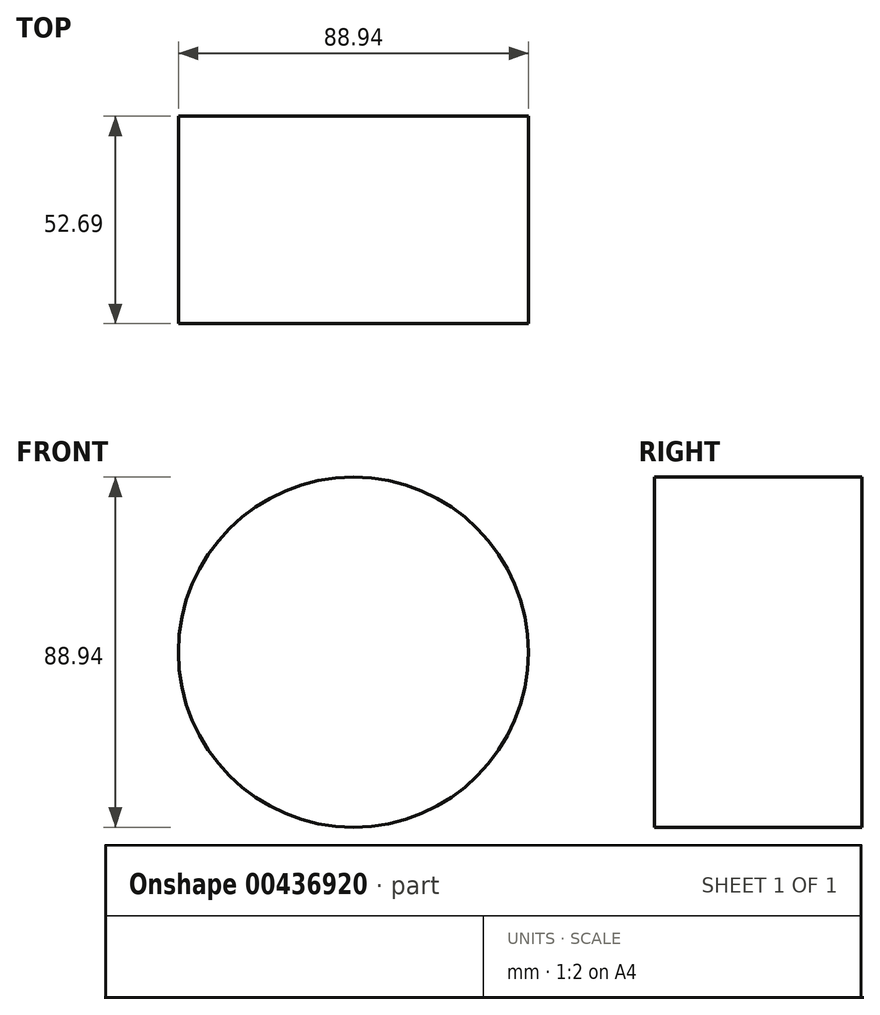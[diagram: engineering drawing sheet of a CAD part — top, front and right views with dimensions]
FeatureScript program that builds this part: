
annotation { "Feature Type Name" : "Feature", "Feature Type Description" : "" }
export const myFeature = defineFeature(function(context is Context, id is Id, definition is map)
    precondition{}
    {
        {
            var Q0;
            Q0=qCreatedBy(makeId("Front.planeOp"),FACE);
            var sketch = newSketch(context, id + "F0", { "sketchPlane" : qUnion([Q0])});
            skCircle(sketch, "E0", {"center": v(0, 0) * mm, "radius": 44.47 * mm});
            skSolve(sketch);
        }
        {
            var Q0;
            Q0=makeQuery(id+"F0.imprint","IMPRINT",FACE,{"disambiguationData":[TD([[makeQuery(id+"F0.imprint","IMPRINT",EDGE,{"derivedFrom":sQuery(id+"F0.wireOp",EDGE,"E0")}),1.0]])]});
            extrude(context, id + "F1", {"entities" : qUnion([Q0]), "depth" : 52.7 * mm});
        }
    });
